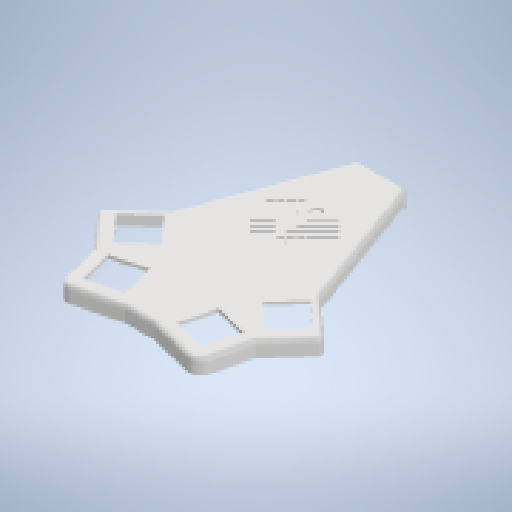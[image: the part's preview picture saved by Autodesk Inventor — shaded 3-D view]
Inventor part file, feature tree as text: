
AUTODESK INVENTOR PART (.ipt)
format: ipt  version: 2024 (Build 280153000, 153)  size: 565,760 bytes
history: native  units: mm
features: reference x36, extrude x6, sketch x6, other x4, mirror x3, plane x2, fillet x1, projected_geometry x1
ambient origin geometry x8: Origin, YZ Plane, XZ Plane, XY Plane, X Axis, Y Axis, Z Axis, Center Point
bodies: Volumenkörper1 (feature_tree)
feature tree (59):
  extrude  "Extrusion1"  Depth=2.0mm
  extrude  "Extrusion2"  Depth=2.0mm
  sketch  "Skizze3"  dims[d4=2.0mm d5=2.0mm]
  plane  "Arbeitsebene1"
  extrude  "Extrusion3"  Depth=2.0mm
  mirror  "Spiegeln1"
  extrude  "Extrusion4"  Depth=2.0mm TaperAngle=0.0deg
  mirror  "Spiegeln2"
  sketch  "Skizze5"  dims[d9=1.5mm d10=0.0mm d12=2.0mm d13=0.0mm]
  plane  "Arbeitsebene2"
  extrude  "Extrusion5"  Depth=2.0mm TaperAngle=0.0deg
  extrude  "Extrusion6"  Depth=2.0mm
  mirror  "Spiegeln3"
  fillet  "Rundung2"  Radius=15.0mm
  sketch  "Skizze1"  dims[d0=19.198622mm d1=2.0mm]
  reference  "Referenz1"
  reference  "Referenz2"
  reference  "Referenz3"
  reference  "Referenz4"
  reference  "Referenz5"
  reference  "Referenz6"
  reference  "Referenz7"
  reference  "Referenz8"
  reference  "Referenz9"
  reference  "Referenz10"
  reference  "Referenz11"
  reference  "Referenz12"
  reference  "Referenz13"
  reference  "Referenz14"
  reference  "Referenz15"
  reference  "Referenz16"
  reference  "Referenz17"
  reference  "Referenz18"
  reference  "Referenz19"
  reference  "Referenz20"
  reference  "Referenz21"
  reference  "Referenz22"
  reference  "Referenz23"
  reference  "Referenz24"
  reference  "Referenz25"
  sketch  "Skizze2"  dims[d2=2.0mm d3=2.0mm]
  projected_geometry  "Projizierte Kontur1"
  reference  "Referenz26"
  reference  "Referenz27"
  sketch  "Skizze4"  dims[d6=2.0mm d7=3.5mm d8=0.0mm]
  reference  "Referenz28"
  reference  "Referenz29"
  reference  "Referenz30"
  reference  "Referenz31"
  reference  "Referenz32"
  reference  "Referenz33"
  reference  "Referenz34"
  reference  "Referenz35"
  reference  "Referenz36"
  sketch  "Skizze6"  dims[d14=15.0mm d15=15.0mm d16=15.0mm d17=15.0mm d18=2.0mm d19=0.0mm d20=5.0mm d21=5.0mm d22=5.0mm d23=5.0mm d24=5.0mm d25=2.9mm d26=2.9mm d27=2.9mm d28=2.9mm d29=2.9mm d30=4.8mm d31=0.0mm d40=1.0mm d41=0.0mm d43=2.0mm]
  other  "Bild1"
  other  "<userpath>\OneDrive\Keyboards\Blavinge\case\case.iam"
  other  "case.iam"
  other  "blavinge:1"
